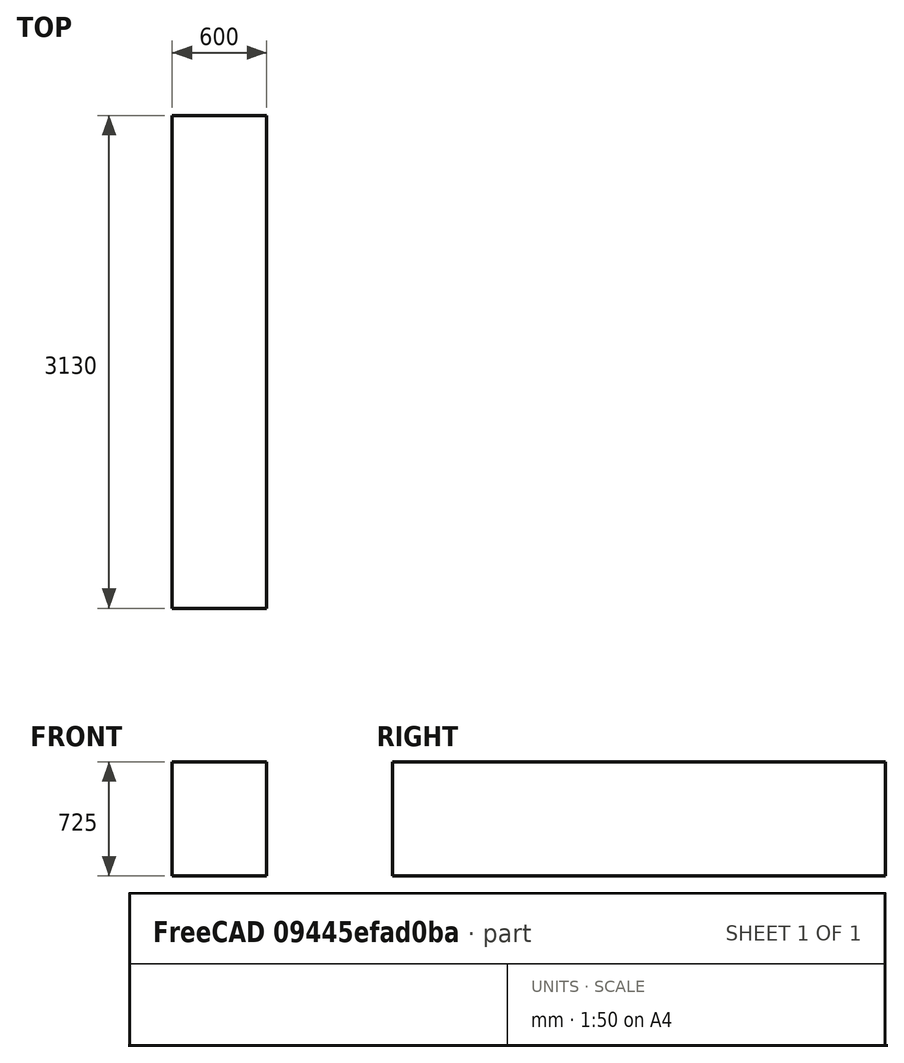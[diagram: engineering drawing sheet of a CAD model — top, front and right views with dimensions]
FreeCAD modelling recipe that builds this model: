
FCSTD DOCUMENT  (FreeCAD 0.19R24276 (Git))
Label: leftBuiltIn
License: All rights reserved
LicenseURL: http://en.wikipedia.org/wiki/All_rights_reserved
objects: Sketcher::SketchObject×1, PartDesign::Pad×1, PartDesign::Body×1
note: 4 computed .brp shape members not serialized (recipe doc carries the construction recipe); baked Part::Feature solids carry a one-line shape summary decoded from their .brp

FEATURE [Sketcher::SketchObject] Sketch
  FullyConstrained = true
  MapMode = 5
  Placement = pos=(0,0,0) rot=(0.57735,0.57735,0.57735;2.0944rad)
  Support = -> [YZ_Plane]
  expr: Constraints[9] = 750 - 25
  sketch-geometry (4):
    g0: LineSegment StartX=0 StartY=0 StartZ=0 EndX=-3130 EndY=0 EndZ=0
    g1: LineSegment StartX=-3130 StartY=0 StartZ=0 EndX=-3130 EndY=725 EndZ=0
    g2: LineSegment StartX=-3130 StartY=725 StartZ=0 EndX=0 EndY=725 EndZ=0
    g3: LineSegment StartX=0 StartY=725 StartZ=0 EndX=0 EndY=0 EndZ=0
  constraints (11):
    c: Coincident(g0,g1)
    c: Coincident(g1,g2)
    c: Coincident(g2,g3)
    c: Coincident(g3,g0)
    c: Horizontal(g0)
    c: Horizontal(g2)
    c: Vertical(g1)
    c: Vertical(g3)
    c: Coincident(g0,g-1)
    c: DistanceY(g1,g1) = 725
    c: DistanceX(g0,g0) = 3130
FEATURE [PartDesign::Pad] Pad
  Direction = (1,1,1)
  Length = 600
  Length2 = 100
  Placement = pos=(0,0,0) rot=(0.57735,0.57735,0.57735;2.0944rad)
  Profile = -> Sketch
  Type = 0
FEATURE [PartDesign::Body] Body
  Group = -> [Sketch,Pad]
  Origin = -> Origin
  Tip = -> Pad
